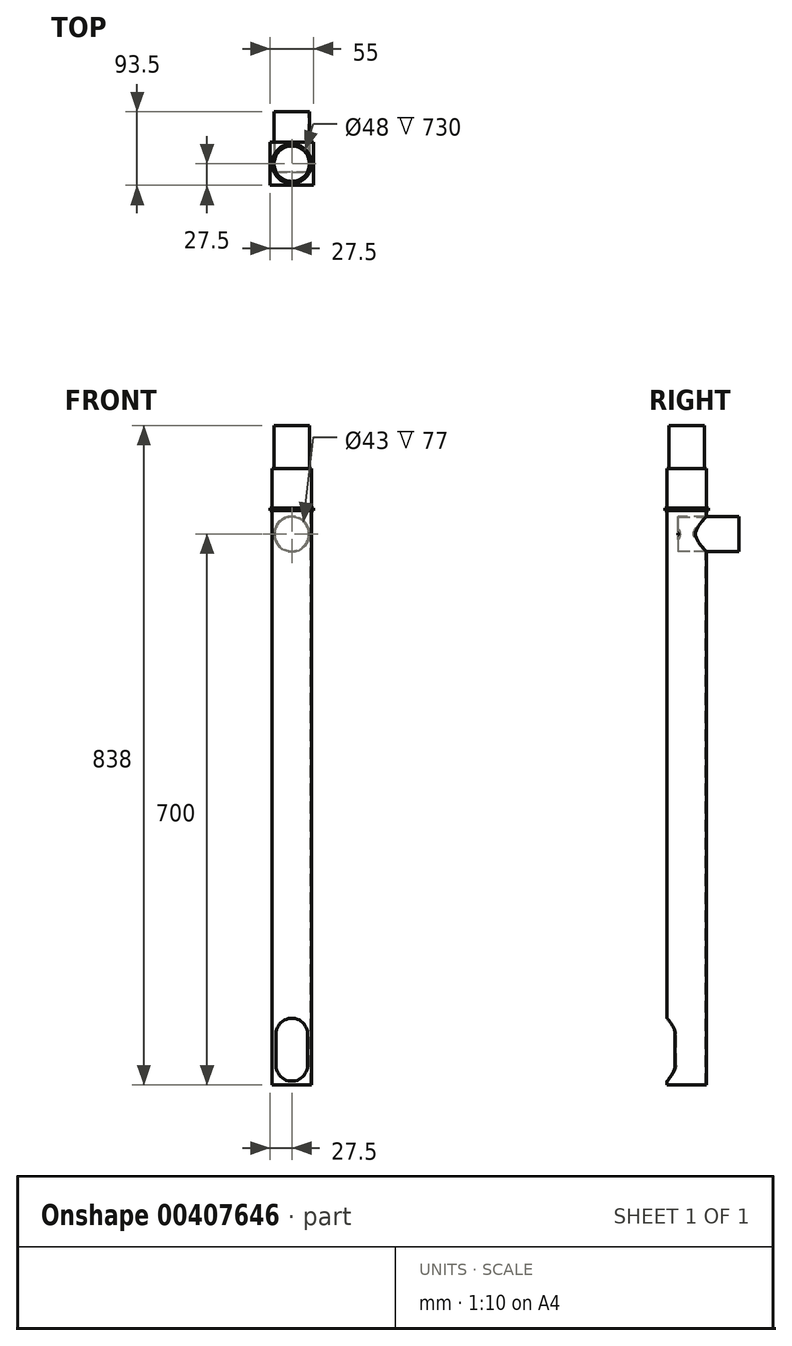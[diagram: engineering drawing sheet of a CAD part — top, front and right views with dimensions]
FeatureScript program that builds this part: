
annotation { "Feature Type Name" : "Feature", "Feature Type Description" : "" }
export const myFeature = defineFeature(function(context is Context, id is Id, definition is map)
    precondition{}
    {
        {
            var Q0;
            Q0=qCreatedBy(makeId("Right.planeOp"),FACE);
            var sketch = newSketch(context, id + "F0", { "sketchPlane" : qUnion([Q0])});
            skLineSegment(sketch, "E0", {"start": v(0, 0) * mm, "end": v(0, 730) * mm});
            skSolve(sketch);
        }
        {
            var Q0;
            Q0=qCreatedBy(makeId("Top.planeOp"),FACE);
            var sketch = newSketch(context, id + "F1", { "sketchPlane" : qUnion([Q0])});
            skCircle(sketch, "E1", {"center": v(0, 0) * mm, "radius": 25 * mm});
            skCircle(sketch, "E2.0", {"center": v(0, 0) * mm, "radius": 24 * mm});
            skSolve(sketch);
        }
        {
            var Q0;
            Q0=makeQuery(id+"F1.imprint","IMPRINT",FACE,{"disambiguationData":[TD([[makeQuery(id+"F1.imprint","IMPRINT",EDGE,{"derivedFrom":sQuery(id+"F1.wireOp",EDGE,"E1")}),1.0]])]});
            var Q1;
            Q1=sQuery(id+"F0.wireOp",EDGE,"E0");
            sweep(context, id + "F2", {"profiles" : qUnion([Q0]), "path" : qUnion([Q1])});
        }
        {
            var Q0;
            Q0=qCreatedBy(makeId("Right.planeOp"),FACE);
            var sketch = newSketch(context, id + "F3", { "sketchPlane" : qUnion([Q0])});
            skLineSegment(sketch, "E3.0", {"start": v(-25, 730) * mm, "end": v(25, 730) * mm});
            skLineSegment(sketch, "E4.bottom", {"start": v(-27.5, 730) * mm, "end": v(27.5, 730) * mm});
            skLineSegment(sketch, "E4.top", {"start": v(-27.5, 733) * mm, "end": v(27.5, 733) * mm});
            skLineSegment(sketch, "E4.left", {"start": v(-27.5, 730) * mm, "end": v(-27.5, 733) * mm});
            skLineSegment(sketch, "E4.right", {"start": v(27.5, 730) * mm, "end": v(27.5, 733) * mm});
            skLineSegment(sketch, "E5", {"start": v(0, 646.95) * mm, "end": v(0, 656.05) * mm, "construction": true});
            skPoint(sketch, "E5.endSnap0", {"position": v(0, 730) * mm});
            skSolve(sketch);
        }
        {
            var Q0;
            Q0=makeQuery(id+"F3.imprint","IMPRINT",FACE,{"disambiguationData":[TD([[makeQuery(id+"F3.imprint","IMPRINT",EDGE,{"derivedFrom":sQuery(id+"F3.wireOp",EDGE,"E4.top")}),-1.0]])]});
            extrude(context, id + "F4", {"entities" : qUnion([Q0]), "operationType" : NewBodyOperationType.ADD, "endBound" : BoundingType.SYMMETRIC, "depth" : 55 * mm});
        }
        {
            var Q0;
            Q0=makeQuery(id+"F4.opExtrude","SWEPT_FACE",FACE,{"disambiguationData":[OSD([sQuery(id+"F3.wireOp",EDGE,"E4.top")])]});
            var sketch = newSketch(context, id + "F5", { "sketchPlane" : qUnion([Q0])});
            skCircle(sketch, "E6", {"center": v(0, 0) * mm, "radius": 25 * mm});
            skSolve(sketch);
        }
        {
            var Q0;
            Q0 = qSketchRegion(id + "F5", true);
            extrude(context, id + "F6", {"entities" : qUnion([Q0]), "operationType" : NewBodyOperationType.ADD, "depth" : 50 * mm});
        }
        {
            var Q0;
            Q0=makeQuery(id+"F6.opExtrude","CAP_FACE",FACE,{"disambiguationData":[OSD([sQuery(id+"F5.wireOp",EDGE,"E6")])],"isStart":false});
            var sketch = newSketch(context, id + "F7", { "sketchPlane" : qUnion([Q0])});
            skCircle(sketch, "E7", {"center": v(0, 0) * mm, "radius": 22.5 * mm});
            skSolve(sketch);
        }
        {
            var Q0;
            Q0 = qSketchRegion(id + "F7", true);
            extrude(context, id + "F8", {"entities" : qUnion([Q0]), "operationType" : NewBodyOperationType.ADD, "depth" : 55 * mm});
        }
        {
            var Q0;
            Q0=makeQuery(id+"F4.opExtrude","SWEPT_FACE",FACE,{"disambiguationData":[OSD([sQuery(id+"F3.wireOp",EDGE,"E4.right")])]});
            var sketch = newSketch(context, id + "F9", { "sketchPlane" : qUnion([Q0])});
            skCircle(sketch, "E8", {"center": v(0, 700) * mm, "radius": 22.5 * mm});
            skCircle(sketch, "E9.0", {"center": v(0, 700) * mm, "radius": 21.5 * mm});
            skSolve(sketch);
        }
        {
            var Q0;
            Q0=makeQuery(id+"F9.imprint","IMPRINT",FACE,{"disambiguationData":[TD([[makeQuery(id+"F9.imprint","IMPRINT",EDGE,{"derivedFrom":sQuery(id+"F9.wireOp",EDGE,"E9.0")}),1.0]])]});
            extrude(context, id + "F10", {"entities" : qUnion([Q0]), "operationType" : NewBodyOperationType.REMOVE, "oppositeDirection" : true, "depth" : 20 * mm});
        }
        {
            var Q0;
            Q0=makeQuery(id+"F9.imprint","IMPRINT",FACE,{"disambiguationData":[TD([[makeQuery(id+"F9.imprint","IMPRINT",EDGE,{"derivedFrom":sQuery(id+"F9.wireOp",EDGE,"E8")}),1.0]])]});
            extrude(context, id + "F11", {"entities" : qUnion([Q0]), "operationType" : NewBodyOperationType.ADD, "endBound" : BoundingType.SYMMETRIC, "depth" : 77 * mm});
        }
        {
            var Q0;
            Q0=makeQuery(id+"F4.opExtrude","SWEPT_FACE",FACE,{"disambiguationData":[OSD([sQuery(id+"F3.wireOp",EDGE,"E4.left")])]});
            var sketch = newSketch(context, id + "F12", { "sketchPlane" : qUnion([Q0])});
            skLineSegment(sketch, "E10", {"start": v(25, 650) * mm, "end": v(25, 0) * mm});
            skLineSegment(sketch, "E11", {"start": v(-25, 0) * mm, "end": v(-25, 650) * mm});
            skArc(sketch, "E12", {"start": v(-20, 25) * mm, "mid": v(0, 5) * mm, "end": v(20, 25) * mm});
            skArc(sketch, "E13", {"start": v(20, 65) * mm, "mid": v(0, 85) * mm, "end": v(-20, 65) * mm});
            skLineSegment(sketch, "E14", {"start": v(-20, 65) * mm, "end": v(-20, 25) * mm});
            skLineSegment(sketch, "E15", {"start": v(20, 65) * mm, "end": v(20, 25) * mm});
            skSolve(sketch);
        }
        {
            var Q0;
            Q0 = qSketchRegion(id + "F12", true);
            extrude(context, id + "F13", {"entities" : qUnion([Q0]), "operationType" : NewBodyOperationType.REMOVE, "oppositeDirection" : true, "depth" : (77 / 2) * mm});
        }
    });
